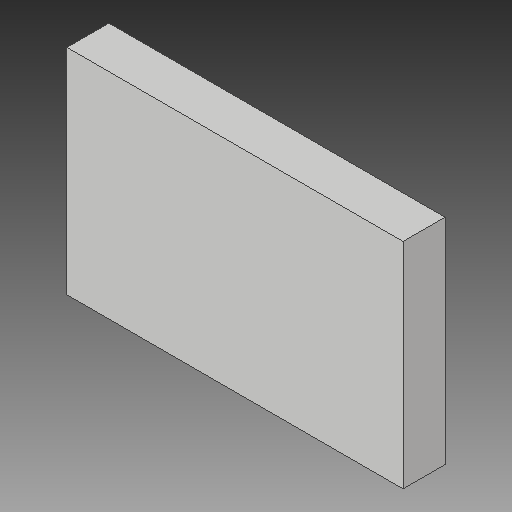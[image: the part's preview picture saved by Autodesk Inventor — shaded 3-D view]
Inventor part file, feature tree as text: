
AUTODESK INVENTOR PART (.ipt)
format: ipt  version: 2017 (Build 210142000, 142)  size: 83,456 bytes
history: native  units: in
note: dims shown in document units (in); Inventor stores cm internally (conversion verified against a paired STEP export)
features: extrude x1, sketch x1
ambient origin geometry x8: Origin, YZ Plane, XZ Plane, XY Plane, X Axis, Y Axis, Z Axis, Center Point
bodies: Solid1 (feature_tree)
feature tree (2):
  extrude  "Extrusion1"  Depth=2.55in
  sketch  "Sketch1"  dims[d0=4.0in d1=2.55in d2=0.5in d3=0.0in]
